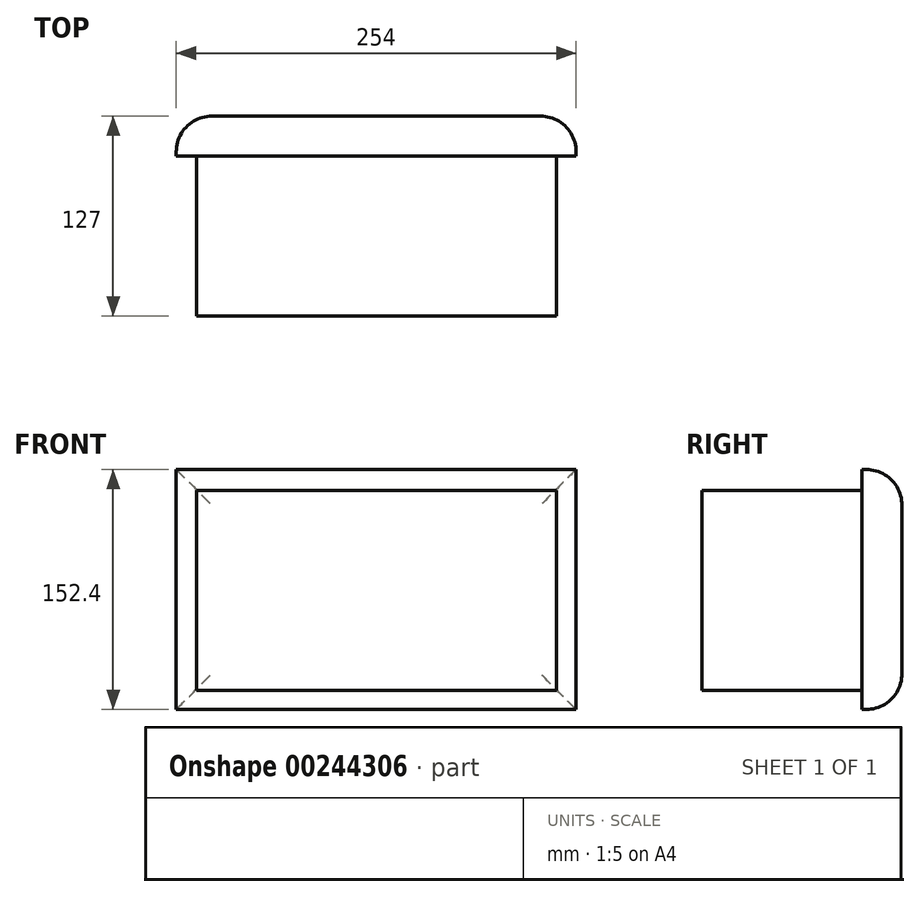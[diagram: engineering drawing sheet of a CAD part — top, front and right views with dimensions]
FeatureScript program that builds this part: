
annotation { "Feature Type Name" : "Feature", "Feature Type Description" : "" }
export const myFeature = defineFeature(function(context is Context, id is Id, definition is map)
    precondition{}
    {
        {
            var Q0;
            Q0=qCreatedBy(makeId("Front.planeOp"),FACE);
            var sketch = newSketch(context, id + "F0", { "sketchPlane" : qUnion([Q0])});
            skLineSegment(sketch, "E0.bottom", {"start": v(97.64, 78.66) * mm, "end": v(-156.36, 78.66) * mm});
            skLineSegment(sketch, "E0.top", {"start": v(97.64, -73.74) * mm, "end": v(-156.36, -73.74) * mm});
            skLineSegment(sketch, "E0.left", {"start": v(97.64, 78.66) * mm, "end": v(97.64, -73.74) * mm});
            skLineSegment(sketch, "E0.right", {"start": v(-156.36, 78.66) * mm, "end": v(-156.36, -73.74) * mm});
            skSolve(sketch);
        }
        {
            var Q0;
            Q0 = qSketchRegion(id + "F0", true);
            extrude(context, id + "F1", {"entities" : qUnion([Q0]), "depth" : 25.4 * mm});
        }
        {
            var Q0;
            Q0=makeQuery(id+"F1.opExtrude","CAP_FACE",FACE,{"disambiguationData":[OSD([sQuery(id+"F0.wireOp",EDGE,"E0.bottom"),sQuery(id+"F0.wireOp",EDGE,"E0.top"),sQuery(id+"F0.wireOp",EDGE,"E0.left"),sQuery(id+"F0.wireOp",EDGE,"E0.right")])],"isStart":true});
            fillet(context, id + "F2", {"entities" : qUnion([Q0]), "radius" : 22.7 * mm, "tangentPropagation" : true, "allowEdgeOverflow" : false});
        }
        {
            var Q0;
            Q0=makeQuery(id+"F1.opExtrude","CAP_FACE",FACE,{"disambiguationData":[OSD([sQuery(id+"F0.wireOp",EDGE,"E0.bottom"),sQuery(id+"F0.wireOp",EDGE,"E0.top"),sQuery(id+"F0.wireOp",EDGE,"E0.left"),sQuery(id+"F0.wireOp",EDGE,"E0.right")])],"isStart":false});
            var sketch = newSketch(context, id + "F3", { "sketchPlane" : qUnion([Q0])});
            skLineSegment(sketch, "E1.bottom", {"start": v(-143.5, 65.2) * mm, "end": v(85.1, 65.2) * mm});
            skLineSegment(sketch, "E1.top", {"start": v(-143.5, -61.8) * mm, "end": v(85.1, -61.8) * mm});
            skLineSegment(sketch, "E1.left", {"start": v(-143.5, 65.2) * mm, "end": v(-143.5, -61.8) * mm});
            skLineSegment(sketch, "E1.right", {"start": v(85.1, 65.2) * mm, "end": v(85.1, -61.8) * mm});
            skSolve(sketch);
        }
        {
            var Q0;
            Q0 = qSketchRegion(id + "F3", true);
            extrude(context, id + "F4", {"entities" : qUnion([Q0]), "operationType" : NewBodyOperationType.ADD, "depth" : 101.6 * mm});
        }
    });
